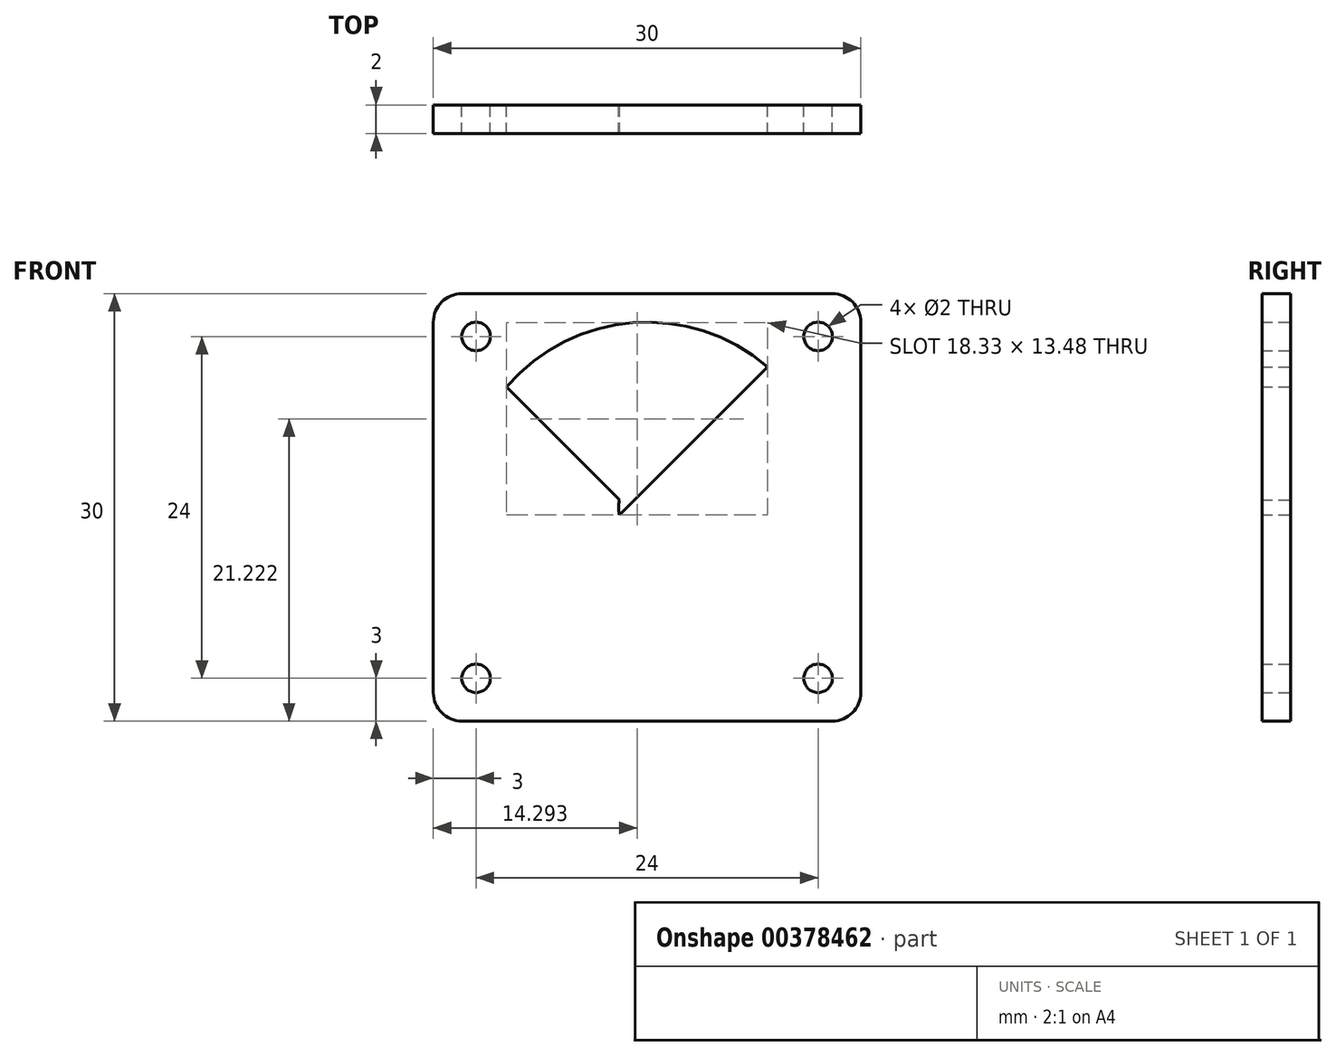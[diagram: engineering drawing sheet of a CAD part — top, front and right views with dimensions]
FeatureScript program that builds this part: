
annotation { "Feature Type Name" : "Feature", "Feature Type Description" : "" }
export const myFeature = defineFeature(function(context is Context, id is Id, definition is map)
    precondition{}
    {
        {
            var Q0;
            Q0=qCreatedBy(makeId("Front.planeOp"),FACE);
            var sketch = newSketch(context, id + "F0", { "sketchPlane" : qUnion([Q0])});
            skLineSegment(sketch, "E0.bottom", {"start": v(12, -12) * mm, "end": v(-12, -12) * mm, "construction": true});
            skLineSegment(sketch, "E0.top", {"start": v(12, 12) * mm, "end": v(-12, 12) * mm, "construction": true});
            skLineSegment(sketch, "E0.left", {"start": v(12, -12) * mm, "end": v(12, 12) * mm, "construction": true});
            skLineSegment(sketch, "E0.right", {"start": v(-12, -12) * mm, "end": v(-12, 12) * mm, "construction": true});
            skPoint(sketch, "E0.middle", {"position": v(0, 0) * mm});
            skCircle(sketch, "E1", {"center": v(-12, 12) * mm, "radius": 1 * mm});
            skCircle(sketch, "E2", {"center": v(12, 12) * mm, "radius": 1 * mm});
            skCircle(sketch, "E3", {"center": v(12, -12) * mm, "radius": 1 * mm});
            skCircle(sketch, "E4", {"center": v(-12, -12) * mm, "radius": 1 * mm});
            skLineSegment(sketch, "E5.bottom", {"start": v(13, -15) * mm, "end": v(-13, -15) * mm});
            skLineSegment(sketch, "E5.top", {"start": v(13, 15) * mm, "end": v(-13, 15) * mm});
            skLineSegment(sketch, "E5.left", {"start": v(15, -13) * mm, "end": v(15, 13) * mm});
            skLineSegment(sketch, "E5.right", {"start": v(-15, -13) * mm, "end": v(-15, 13) * mm});
            skCircle(sketch, "E6", {"center": v(0, 0) * mm, "radius": 13 * mm});
            skLineSegment(sketch, "E7", {"start": v(-12.7, 11.3) * mm, "end": v(11.3, -12.7) * mm});
            skLineSegment(sketch, "E8", {"start": v(-11.3, 12.7) * mm, "end": v(12.7, -11.3) * mm});
            skLineSegment(sketch, "E9", {"start": v(12.7, 11.3) * mm, "end": v(-11.3, -12.7) * mm});
            skLineSegment(sketch, "E10", {"start": v(-12.7, -11.3) * mm, "end": v(11.3, 12.7) * mm});
            skCircle(sketch, "E11", {"center": v(0, 0) * mm, "radius": 2 * mm});
            skPoint(sketch, "E12.visualSharp", {"position": v(-15, 15) * mm});
            skArc(sketch, "E12.filletArc", {"start": v(-13, 15) * mm, "mid": v(-14.41, 14.41) * mm, "end": v(-15, 13) * mm});
            skPoint(sketch, "E13.visualSharp", {"position": v(15, 15) * mm});
            skArc(sketch, "E13.filletArc", {"start": v(15, 13) * mm, "mid": v(14.41, 14.41) * mm, "end": v(13, 15) * mm});
            skPoint(sketch, "E14.visualSharp", {"position": v(15, -15) * mm});
            skArc(sketch, "E14.filletArc", {"start": v(13, -15) * mm, "mid": v(14.41, -14.41) * mm, "end": v(15, -13) * mm});
            skPoint(sketch, "E15.visualSharp", {"position": v(-15, -15) * mm});
            skArc(sketch, "E15.filletArc", {"start": v(-15, -13) * mm, "mid": v(-14.41, -14.41) * mm, "end": v(-13, -15) * mm});
            skSolve(sketch);
        }
        {
            var Q0;
            Q0=makeQuery(id+"F0.imprint","IMPRINT",FACE,{"disambiguationData":[TD([[makeQuery(id+"F0.imprint","IMPRINT",EDGE,{"derivedFrom":sQuery(id+"F0.wireOp",EDGE,"E5.bottom")}),-1.0]])]});
            var Q1;
            {var subQ0=sQuery(id+"F0.wireOp",EDGE,"E7");var subQ1=sQuery(id+"F0.wireOp",EDGE,"E1");var subQ2=makeQuery(id+"F0.imprint","INTERSECT",VERTEX,{"derivedFrom":[subQ1,subQ0]});Q1=makeQuery(id+"F0.imprint","IMPRINT",FACE,{"disambiguationData":[TD([[makeQuery(id+"F0.imprint","IMPRINT",EDGE,{"disambiguationData":[TD([[subQ2,-1.0]])],"derivedFrom":subQ1}),-1.0]])]});}
            var Q2;
            {var subQ0=sQuery(id+"F0.wireOp",EDGE,"E8");var subQ1=sQuery(id+"F0.wireOp",EDGE,"E6");var subQ2=makeQuery(id+"F0.imprint","INTERSECT",VERTEX,{"disambiguationData":[OD(0.0)],"derivedFrom":[subQ1,subQ0]});Q2=makeQuery(id+"F0.imprint","IMPRINT",FACE,{"disambiguationData":[TD([[makeQuery(id+"F0.imprint","IMPRINT",EDGE,{"disambiguationData":[TD([[subQ2,-1.0]])],"derivedFrom":subQ1}),1.0]])]});}
            var Q3;
            {var subQ0=sQuery(id+"F0.wireOp",EDGE,"E11");var subQ1=sQuery(id+"F0.wireOp",EDGE,"E8");var subQ2=makeQuery(id+"F0.imprint","INTERSECT",VERTEX,{"disambiguationData":[OD(0.0)],"derivedFrom":[subQ1,subQ0]});Q3=makeQuery(id+"F0.imprint","IMPRINT",FACE,{"disambiguationData":[TD([[makeQuery(id+"F0.imprint","IMPRINT",EDGE,{"disambiguationData":[TD([[subQ2,-1.0]])],"derivedFrom":subQ1}),1.0]])]});}
            var Q4;
            {var subQ0=sQuery(id+"F0.wireOp",EDGE,"E9");var subQ1=sQuery(id+"F0.wireOp",EDGE,"E7");var subQ2=makeQuery(id+"F0.imprint","INTERSECT",VERTEX,{"derivedFrom":[subQ1,subQ0]});Q4=makeQuery(id+"F0.imprint","IMPRINT",FACE,{"disambiguationData":[TD([[makeQuery(id+"F0.imprint","IMPRINT",EDGE,{"disambiguationData":[TD([[subQ2,-1.0]])],"derivedFrom":subQ1}),1.0]])]});}
            var Q5;
            {var subQ0=sQuery(id+"F0.wireOp",EDGE,"E11");var subQ1=sQuery(id+"F0.wireOp",EDGE,"E7");var subQ2=makeQuery(id+"F0.imprint","INTERSECT",VERTEX,{"disambiguationData":[OD(0.0)],"derivedFrom":[subQ1,subQ0]});Q5=makeQuery(id+"F0.imprint","IMPRINT",FACE,{"disambiguationData":[TD([[makeQuery(id+"F0.imprint","IMPRINT",EDGE,{"disambiguationData":[TD([[subQ2,-1.0]])],"derivedFrom":subQ1}),1.0]])]});}
            var Q6;
            {var subQ0=sQuery(id+"F0.wireOp",EDGE,"E7");var subQ1=sQuery(id+"F0.wireOp",EDGE,"E3");var subQ2=makeQuery(id+"F0.imprint","INTERSECT",VERTEX,{"derivedFrom":[subQ1,subQ0]});Q6=makeQuery(id+"F0.imprint","IMPRINT",FACE,{"disambiguationData":[TD([[makeQuery(id+"F0.imprint","IMPRINT",EDGE,{"disambiguationData":[TD([[subQ2,1.0]])],"derivedFrom":subQ1}),-1.0]])]});}
            var Q7;
            {var subQ0=sQuery(id+"F0.wireOp",EDGE,"E10");var subQ1=sQuery(id+"F0.wireOp",EDGE,"E6");var subQ2=makeQuery(id+"F0.imprint","INTERSECT",VERTEX,{"disambiguationData":[OD(0.0)],"derivedFrom":[subQ1,subQ0]});Q7=makeQuery(id+"F0.imprint","IMPRINT",FACE,{"disambiguationData":[TD([[makeQuery(id+"F0.imprint","IMPRINT",EDGE,{"disambiguationData":[TD([[subQ2,1.0]])],"derivedFrom":subQ1}),1.0]])]});}
            var Q8;
            {var subQ0=sQuery(id+"F0.wireOp",EDGE,"E9");var subQ1=sQuery(id+"F0.wireOp",EDGE,"E8");var subQ2=makeQuery(id+"F0.imprint","INTERSECT",VERTEX,{"derivedFrom":[subQ1,subQ0]});Q8=makeQuery(id+"F0.imprint","IMPRINT",FACE,{"disambiguationData":[TD([[makeQuery(id+"F0.imprint","IMPRINT",EDGE,{"disambiguationData":[TD([[subQ2,-1.0]])],"derivedFrom":subQ1}),1.0]])]});}
            var Q9;
            {var subQ0=sQuery(id+"F0.wireOp",EDGE,"E11");var subQ1=sQuery(id+"F0.wireOp",EDGE,"E7");var subQ2=makeQuery(id+"F0.imprint","INTERSECT",VERTEX,{"disambiguationData":[OD(0.0)],"derivedFrom":[subQ1,subQ0]});Q9=makeQuery(id+"F0.imprint","IMPRINT",FACE,{"disambiguationData":[TD([[makeQuery(id+"F0.imprint","IMPRINT",EDGE,{"disambiguationData":[TD([[subQ2,-1.0]])],"derivedFrom":subQ1}),-1.0]])]});}
            var Q10;
            {var subQ0=sQuery(id+"F0.wireOp",EDGE,"E10");var subQ1=sQuery(id+"F0.wireOp",EDGE,"E7");var subQ2=makeQuery(id+"F0.imprint","INTERSECT",VERTEX,{"derivedFrom":[subQ1,subQ0]});Q10=makeQuery(id+"F0.imprint","IMPRINT",FACE,{"disambiguationData":[TD([[makeQuery(id+"F0.imprint","IMPRINT",EDGE,{"disambiguationData":[TD([[subQ2,-1.0]])],"derivedFrom":subQ1}),1.0]])]});}
            var Q11;
            {var subQ0=sQuery(id+"F0.wireOp",EDGE,"E10");var subQ1=sQuery(id+"F0.wireOp",EDGE,"E7");var subQ2=makeQuery(id+"F0.imprint","INTERSECT",VERTEX,{"derivedFrom":[subQ1,subQ0]});Q11=makeQuery(id+"F0.imprint","IMPRINT",FACE,{"disambiguationData":[TD([[makeQuery(id+"F0.imprint","IMPRINT",EDGE,{"disambiguationData":[TD([[subQ2,-1.0]])],"derivedFrom":subQ1}),-1.0]])]});}
            var Q12;
            {var subQ0=sQuery(id+"F0.wireOp",EDGE,"E9");var subQ1=sQuery(id+"F0.wireOp",EDGE,"E4");var subQ2=makeQuery(id+"F0.imprint","INTERSECT",VERTEX,{"derivedFrom":[subQ1,subQ0]});Q12=makeQuery(id+"F0.imprint","IMPRINT",FACE,{"disambiguationData":[TD([[makeQuery(id+"F0.imprint","IMPRINT",EDGE,{"disambiguationData":[TD([[subQ2,-1.0]])],"derivedFrom":subQ1}),-1.0]])]});}
            var Q13;
            {var subQ0=sQuery(id+"F0.wireOp",EDGE,"E9");var subQ1=sQuery(id+"F0.wireOp",EDGE,"E2");var subQ2=makeQuery(id+"F0.imprint","INTERSECT",VERTEX,{"derivedFrom":[subQ1,subQ0]});Q13=makeQuery(id+"F0.imprint","IMPRINT",FACE,{"disambiguationData":[TD([[makeQuery(id+"F0.imprint","IMPRINT",EDGE,{"disambiguationData":[TD([[subQ2,1.0]])],"derivedFrom":subQ1}),-1.0]])]});}
            var Q14;
            {var subQ0=sQuery(id+"F0.wireOp",EDGE,"E9");var subQ1=sQuery(id+"F0.wireOp",EDGE,"E7");var subQ2=makeQuery(id+"F0.imprint","INTERSECT",VERTEX,{"derivedFrom":[subQ1,subQ0]});Q14=makeQuery(id+"F0.imprint","IMPRINT",FACE,{"disambiguationData":[TD([[makeQuery(id+"F0.imprint","IMPRINT",EDGE,{"disambiguationData":[TD([[subQ2,-1.0]])],"derivedFrom":subQ1}),-1.0]])]});}
            var Q15;
            {var subQ0=sQuery(id+"F0.wireOp",EDGE,"E10");var subQ1=sQuery(id+"F0.wireOp",EDGE,"E8");var subQ2=makeQuery(id+"F0.imprint","INTERSECT",VERTEX,{"derivedFrom":[subQ1,subQ0]});Q15=makeQuery(id+"F0.imprint","IMPRINT",FACE,{"disambiguationData":[TD([[makeQuery(id+"F0.imprint","IMPRINT",EDGE,{"disambiguationData":[TD([[subQ2,-1.0]])],"derivedFrom":subQ1}),1.0]])]});}
            var Q16;
            {var subQ0=sQuery(id+"F0.wireOp",EDGE,"E10");var subQ1=sQuery(id+"F0.wireOp",EDGE,"E6");var subQ2=makeQuery(id+"F0.imprint","INTERSECT",VERTEX,{"disambiguationData":[OD(1.0)],"derivedFrom":[subQ1,subQ0]});Q16=makeQuery(id+"F0.imprint","IMPRINT",FACE,{"disambiguationData":[TD([[makeQuery(id+"F0.imprint","IMPRINT",EDGE,{"disambiguationData":[TD([[subQ2,-1.0]])],"derivedFrom":subQ1}),1.0]])]});}
            var Q17;
            {var subQ0=sQuery(id+"F0.wireOp",EDGE,"E7");var subQ1=sQuery(id+"F0.wireOp",EDGE,"E6");var subQ2=makeQuery(id+"F0.imprint","INTERSECT",VERTEX,{"disambiguationData":[OD(1.0)],"derivedFrom":[subQ1,subQ0]});Q17=makeQuery(id+"F0.imprint","IMPRINT",FACE,{"disambiguationData":[TD([[makeQuery(id+"F0.imprint","IMPRINT",EDGE,{"disambiguationData":[TD([[subQ2,-1.0]])],"derivedFrom":subQ1}),1.0]])]});}
            extrude(context, id + "F1", {"entities" : qUnion([Q0, Q1, Q2, Q3, Q4, Q5, Q6, Q7, Q8, Q9, Q10, Q11, Q12, Q13, Q14, Q15, Q16, Q17]), "depth" : 2 * mm});
        }
    });
